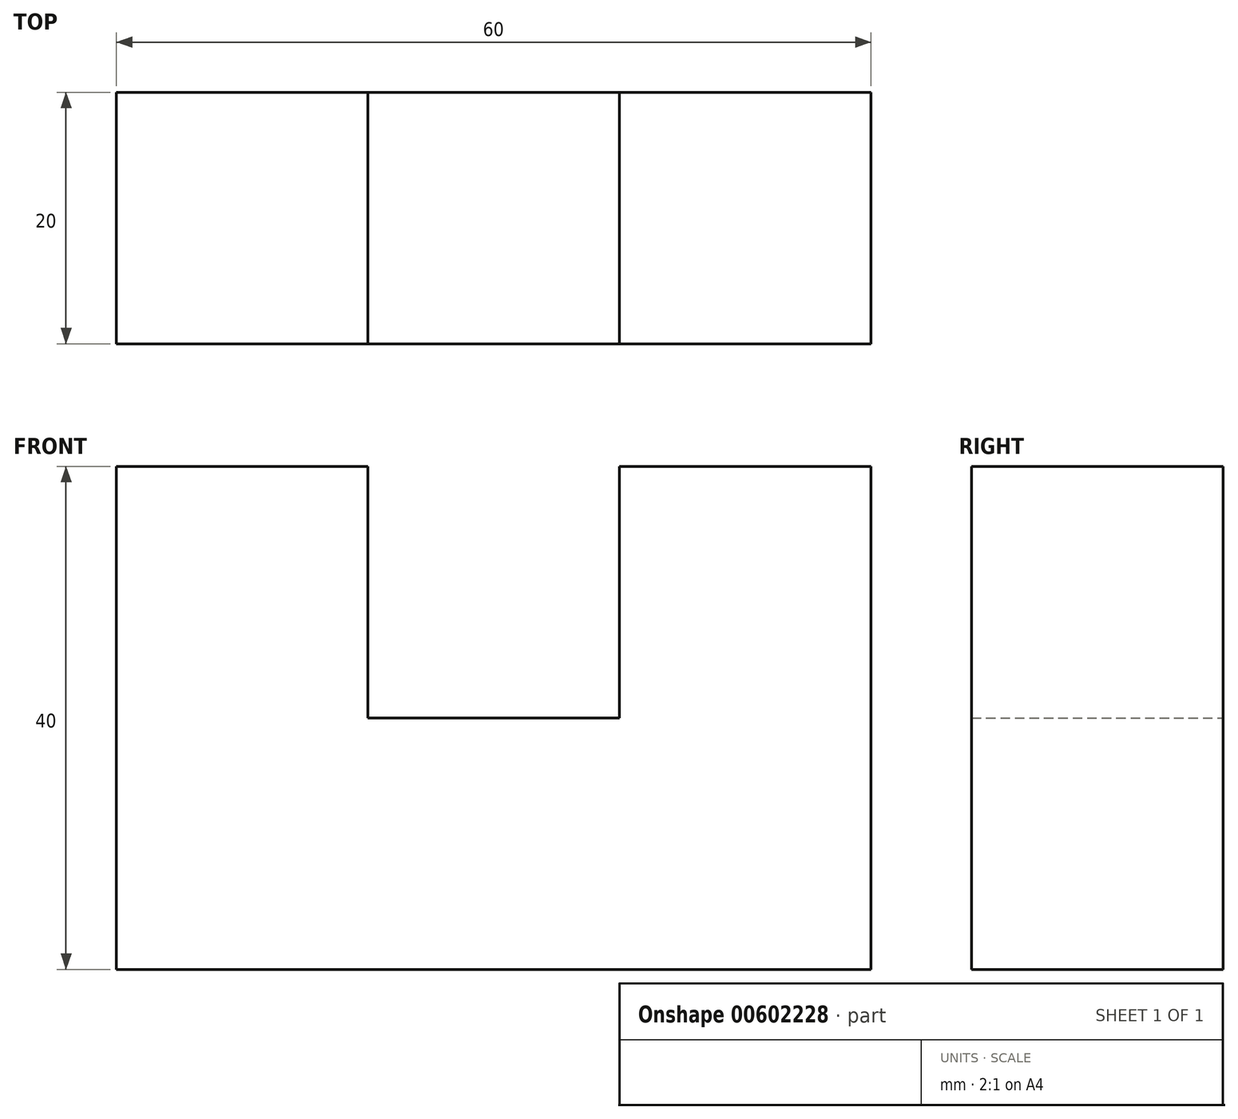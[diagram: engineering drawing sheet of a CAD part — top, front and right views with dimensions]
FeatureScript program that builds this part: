
annotation { "Feature Type Name" : "Feature", "Feature Type Description" : "" }
export const myFeature = defineFeature(function(context is Context, id is Id, definition is map)
    precondition{}
    {
        {
            var Q0;
            Q0=qCreatedBy(makeId("Front.planeOp"),FACE);
            var sketch = newSketch(context, id + "F0", { "sketchPlane" : qUnion([Q0])});
            skLineSegment(sketch, "E0", {"start": v(-44.58, 43.02) * mm, "end": v(-44.58, 3.02) * mm});
            skLineSegment(sketch, "E1", {"start": v(-44.58, 3.02) * mm, "end": v(15.42, 3.02) * mm});
            skLineSegment(sketch, "E2", {"start": v(15.42, 3.02) * mm, "end": v(15.42, 43.02) * mm});
            skLineSegment(sketch, "E3", {"start": v(15.42, 43.02) * mm, "end": v(-4.58, 43.02) * mm});
            skLineSegment(sketch, "E4", {"start": v(-4.58, 43.02) * mm, "end": v(-4.58, 23.02) * mm});
            skLineSegment(sketch, "E5", {"start": v(-4.58, 23.02) * mm, "end": v(-24.58, 23.02) * mm});
            skLineSegment(sketch, "E6", {"start": v(-24.58, 23.02) * mm, "end": v(-24.58, 43.02) * mm});
            skLineSegment(sketch, "E7", {"start": v(-24.58, 43.02) * mm, "end": v(-44.58, 43.02) * mm});
            skSolve(sketch);
        }
        {
            var Q0;
            Q0 = qSketchRegion(id + "F0", true);
            extrude(context, id + "F1", {"entities" : qUnion([Q0]), "depth" : 20 * mm, "offsetDistance" : 25 * mm});
        }
    });
